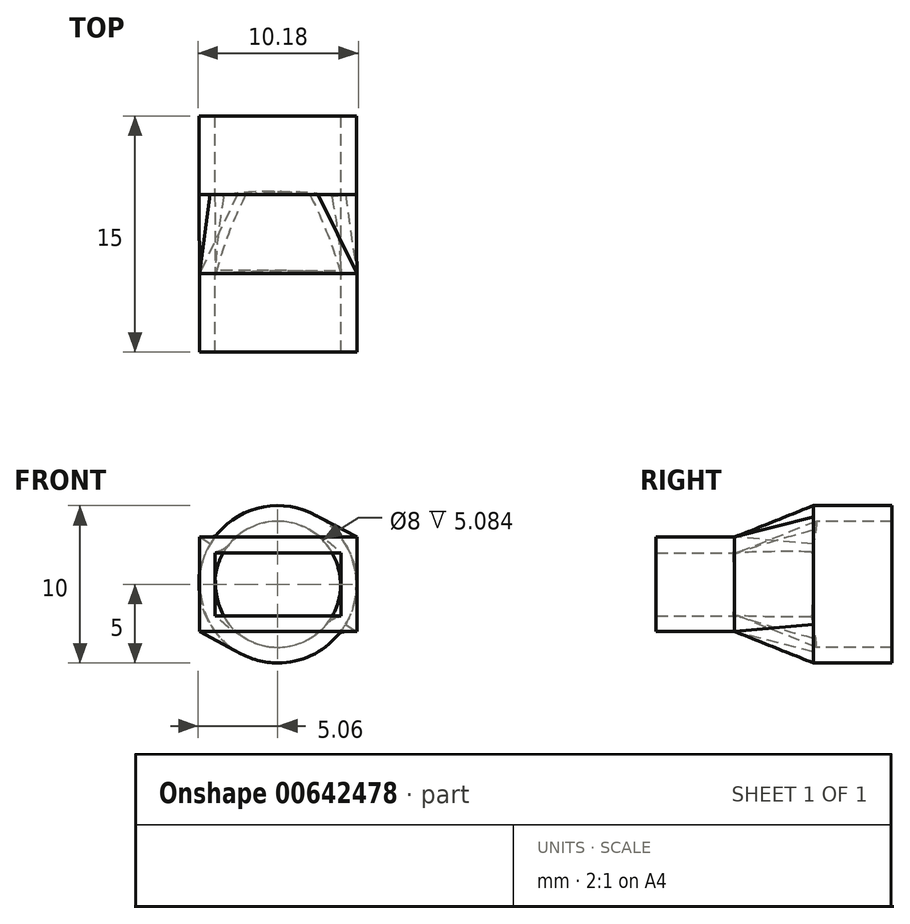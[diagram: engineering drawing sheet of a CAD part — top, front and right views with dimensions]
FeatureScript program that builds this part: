
annotation { "Feature Type Name" : "Feature", "Feature Type Description" : "" }
export const myFeature = defineFeature(function(context is Context, id is Id, definition is map)
    precondition{}
    {
        {
            var Q0;
            Q0=qCreatedBy(makeId("Front.planeOp"),FACE);
            var sketch = newSketch(context, id + "F0", { "sketchPlane" : qUnion([Q0])});
            skCircle(sketch, "E0", {"center": v(-33.21, 0) * mm, "radius": 5 * mm});
            skSolve(sketch);
        }
        {
            var Q0;
            Q0 = qSketchRegion(id + "F0", true);
            extrude(context, id + "F1", {"entities" : qUnion([Q0]), "oppositeDirection" : true, "depth" : 5 * mm, "offsetDistance" : 25 * mm});
        }
        {
            var Q0;
            Q0=qCreatedBy(makeId("Top.planeOp"),FACE);
            var sketch = newSketch(context, id + "F2", { "sketchPlane" : qUnion([Q0])});
            skLineSegment(sketch, "E1", {"start": v(-33.2, -10) * mm, "end": v(-28.2, -10) * mm});
            skLineSegment(sketch, "E2", {"start": v(-28.2, -10) * mm, "end": v(-28.2, -5) * mm});
            skLineSegment(sketch, "E3", {"start": v(-33.2, -10) * mm, "end": v(-38.18, -10) * mm});
            skLineSegment(sketch, "E4", {"start": v(-38.18, -10) * mm, "end": v(-38.18, -5) * mm});
            skLineSegment(sketch, "E5", {"start": v(-38.18, -5) * mm, "end": v(-28.2, -5) * mm});
            skSolve(sketch);
        }
        {
            var Q0;
            Q0 = qSketchRegion(id + "F2", true);
            extrude(context, id + "F3", {"entities" : qUnion([Q0]), "depth" : 3 * mm, "offsetDistance" : 25 * mm, "hasSecondDirection" : true, "secondDirectionOppositeDirection" : true, "secondDirectionDepth" : 3 * mm});
        }
        {
            var Q1;
            Q1=makeQuery(id+"F1.opExtrude","CAP_FACE",FACE,{"disambiguationData":[OSD([sQuery(id+"F0.wireOp",EDGE,"E0")])],"isStart":true});
            var Q2;
            Q2=makeQuery(id+"F3.opExtrude","SWEPT_FACE",FACE,{"disambiguationData":[OSD([sQuery(id+"F2.wireOp",EDGE,"E5")])]});
            loft(context, id + "F4", {"operationType" : NewBodyOperationType.ADD, "sheetProfilesArray" : [{ "sheetProfileEntities" : qUnion([Q1]) }, { "sheetProfileEntities" : qUnion([Q2]) }]});
        }
        {
            var Q0;
            Q0=makeQuery(id+"F3.opExtrude","SWEPT_FACE",FACE,{"disambiguationData":[OSD([sQuery(id+"F2.wireOp",EDGE,"E1"),sQuery(id+"F2.wireOp",EDGE,"E3")])]});
            var Q1;
            Q1=makeQuery(id+"F1.opExtrude","CAP_FACE",FACE,{"disambiguationData":[OSD([sQuery(id+"F0.wireOp",EDGE,"E0")])],"isStart":false});
            shell(context, id + "F5", {"entities" : qUnion([Q0, Q1]), "thickness" : 1 * mm});
        }
    });
